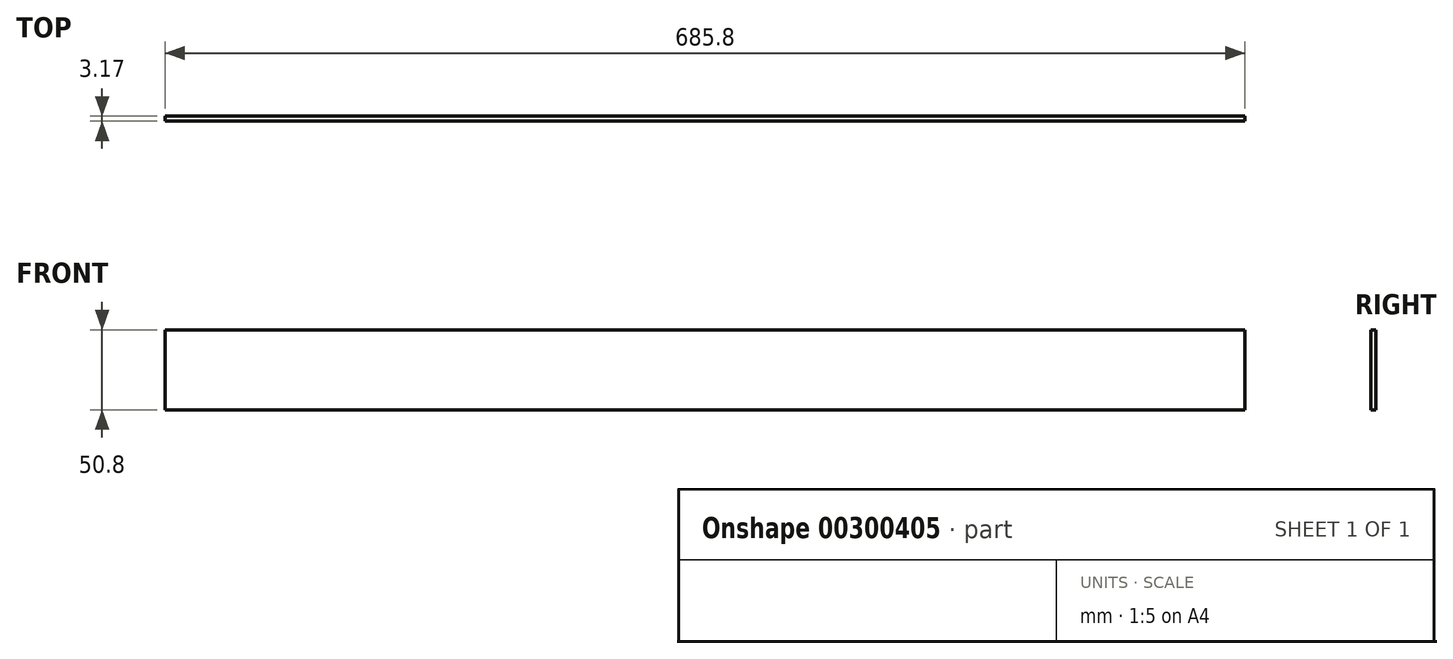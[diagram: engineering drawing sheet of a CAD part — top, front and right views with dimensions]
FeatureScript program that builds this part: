
annotation { "Feature Type Name" : "Feature", "Feature Type Description" : "" }
export const myFeature = defineFeature(function(context is Context, id is Id, definition is map)
    precondition{}
    {
        {
            var Q0;
            Q0=qCreatedBy(makeId("Front.planeOp"),FACE);
            var sketch = newSketch(context, id + "F0", { "sketchPlane" : qUnion([Q0])});
            skLineSegment(sketch, "E0.bottom", {"start": v(342.9, 25.4) * mm, "end": v(-342.9, 25.4) * mm});
            skLineSegment(sketch, "E0.top", {"start": v(342.9, -25.4) * mm, "end": v(-342.9, -25.4) * mm});
            skLineSegment(sketch, "E0.left", {"start": v(342.9, 25.4) * mm, "end": v(342.9, -25.4) * mm});
            skLineSegment(sketch, "E0.right", {"start": v(-342.9, 25.4) * mm, "end": v(-342.9, -25.4) * mm});
            skPoint(sketch, "E0.middle", {"position": v(0, 0) * mm});
            skSolve(sketch);
        }
        {
            var Q0;
            Q0 = qSketchRegion(id + "F0", true);
            extrude(context, id + "F1", {"entities" : qUnion([Q0]), "depth" : 3.17 * mm});
        }
    });
